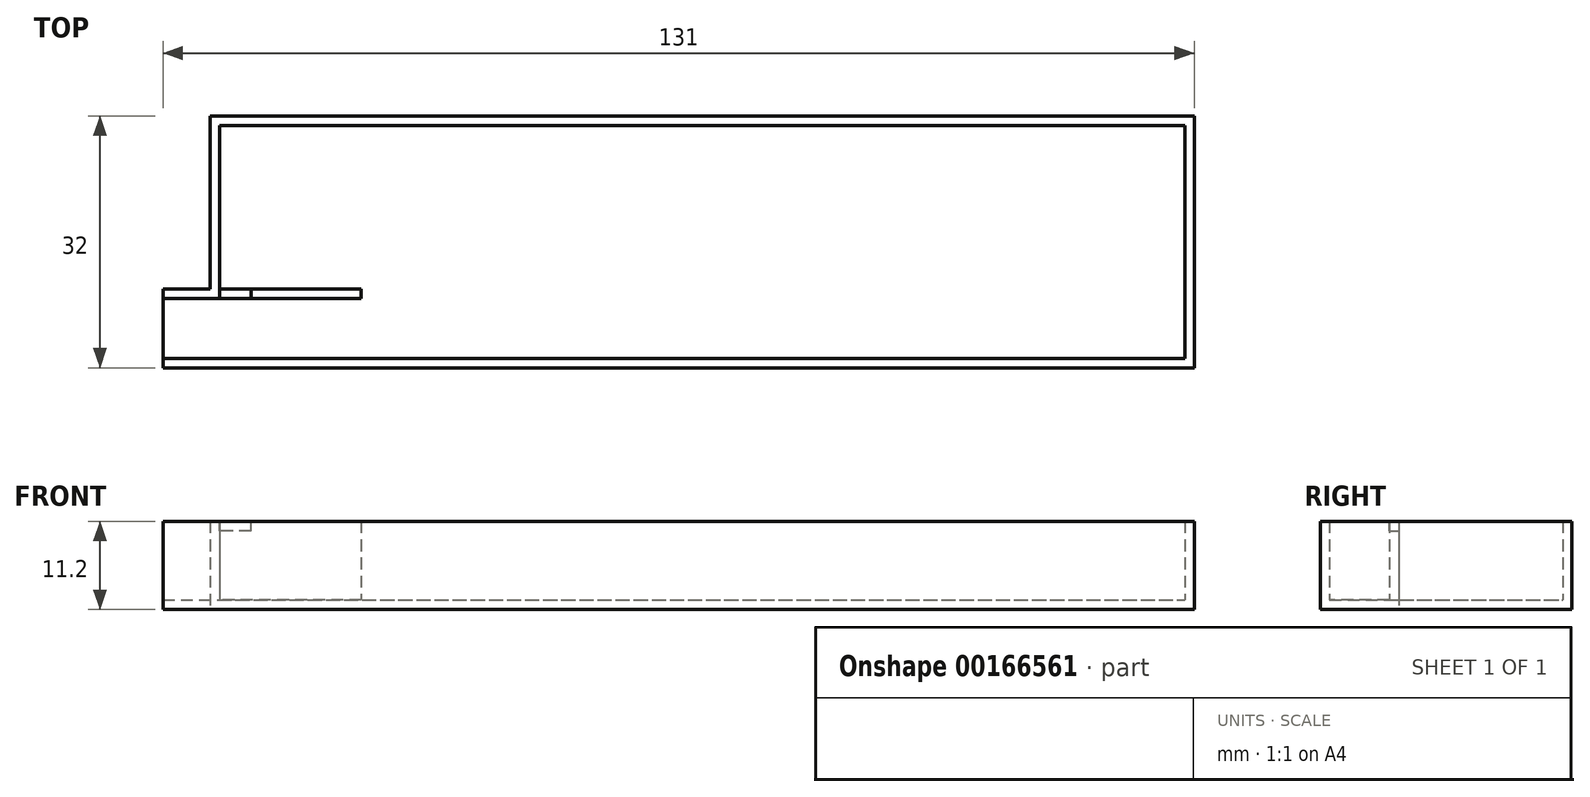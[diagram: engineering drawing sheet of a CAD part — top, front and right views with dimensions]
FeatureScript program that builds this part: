
annotation { "Feature Type Name" : "Feature", "Feature Type Description" : "" }
export const myFeature = defineFeature(function(context is Context, id is Id, definition is map)
    precondition{}
    {
        {
            var Q0;
            Q0=qCreatedBy(makeId("Top.planeOp"),FACE);
            var sketch = newSketch(context, id + "F0", { "sketchPlane" : qUnion([Q0])});
            skLineSegment(sketch, "E0", {"start": v(0, 0) * mm, "end": v(0, 32) * mm});
            skLineSegment(sketch, "E1", {"start": v(0, 32) * mm, "end": v(-125, 32) * mm});
            skLineSegment(sketch, "E2", {"start": v(-125, 32) * mm, "end": v(-125, 10) * mm});
            skLineSegment(sketch, "E3", {"start": v(-125, 10) * mm, "end": v(-131, 10) * mm});
            skLineSegment(sketch, "E4", {"start": v(-131, 10) * mm, "end": v(-131, 0) * mm});
            skLineSegment(sketch, "E5", {"start": v(-131, 0) * mm, "end": v(-125, 0) * mm});
            skLineSegment(sketch, "E6", {"start": v(-125, 0) * mm, "end": v(-125, 0) * mm});
            skLineSegment(sketch, "E7", {"start": v(-125, 0) * mm, "end": v(0, 0) * mm});
            skSolve(sketch);
        }
        {
            var Q0;
            Q0 = qSketchRegion(id + "F0", true);
            extrude(context, id + "F1", {"entities" : qUnion([Q0]), "depth" : 1.2 * mm});
        }
        {
            var Q0;
            Q0=makeQuery(id+"F1.opExtrude","CAP_FACE",FACE,{"disambiguationData":[OSD([sQuery(id+"F0.wireOp",EDGE,"E0"),sQuery(id+"F0.wireOp",EDGE,"E1"),sQuery(id+"F0.wireOp",EDGE,"E2"),sQuery(id+"F0.wireOp",EDGE,"E3"),sQuery(id+"F0.wireOp",EDGE,"E4"),sQuery(id+"F0.wireOp",EDGE,"E5"),sQuery(id+"F0.wireOp",EDGE,"E7")])],"isStart":false});
            var sketch = newSketch(context, id + "F2", { "sketchPlane" : qUnion([Q0])});
            skLineSegment(sketch, "E8", {"start": v(0, 0) * mm, "end": v(-131, 0) * mm});
            skLineSegment(sketch, "E9", {"start": v(-131, 0) * mm, "end": v(-131, 1.2) * mm});
            skLineSegment(sketch, "E10", {"start": v(-131, 10) * mm, "end": v(-131, 8.8) * mm});
            skLineSegment(sketch, "E11", {"start": v(-131, 8.8) * mm, "end": v(-123.8, 8.8) * mm});
            skLineSegment(sketch, "E12", {"start": v(-123.8, 8.8) * mm, "end": v(-123.8, 30.8) * mm});
            skLineSegment(sketch, "E13", {"start": v(-123.8, 30.8) * mm, "end": v(-1.2, 30.8) * mm});
            skLineSegment(sketch, "E14", {"start": v(0, 32) * mm, "end": v(-125, 32) * mm});
            skLineSegment(sketch, "E15", {"start": v(-125, 32) * mm, "end": v(-125, 10) * mm});
            skLineSegment(sketch, "E16", {"start": v(-125, 10) * mm, "end": v(-131, 10) * mm});
            skLineSegment(sketch, "E17", {"start": v(0, 32) * mm, "end": v(0, 0) * mm});
            skLineSegment(sketch, "E18", {"start": v(-131, 1.2) * mm, "end": v(-1.2, 1.2) * mm});
            skLineSegment(sketch, "E19", {"start": v(-1.2, 1.2) * mm, "end": v(-1.2, 30.8) * mm});
            skLineSegment(sketch, "E20", {"start": v(-123.8, 8.8) * mm, "end": v(-105.8, 8.8) * mm});
            skLineSegment(sketch, "E21", {"start": v(-105.8, 8.8) * mm, "end": v(-105.8, 10) * mm});
            skLineSegment(sketch, "E22", {"start": v(-105.8, 10) * mm, "end": v(-123.8, 10) * mm});
            skLineSegment(sketch, "E23", {"start": v(-123.8, 10) * mm, "end": v(-123.8, 8.8) * mm});
            skSolve(sketch);
        }
        {
            var Q0;
            Q0 = qSketchRegion(id + "F2", true);
            extrude(context, id + "F3", {"entities" : qUnion([Q0]), "operationType" : NewBodyOperationType.ADD, "depth" : 10 * mm});
        }
        {
            var Q0;
            Q0=makeQuery(id+"F3.opExtrude","SWEPT_FACE",FACE,{"disambiguationData":[OSD([sQuery(id+"F2.wireOp",EDGE,"E22")])]});
            var sketch = newSketch(context, id + "F4", { "sketchPlane" : qUnion([Q0])});
            skLineSegment(sketch, "E24.bottom", {"start": v(123.8, 11.2) * mm, "end": v(119.8, 11.2) * mm});
            skLineSegment(sketch, "E24.top", {"start": v(123.8, 10) * mm, "end": v(119.8, 10) * mm});
            skLineSegment(sketch, "E24.left", {"start": v(123.8, 11.2) * mm, "end": v(123.8, 10) * mm});
            skLineSegment(sketch, "E24.right", {"start": v(119.8, 11.2) * mm, "end": v(119.8, 10) * mm});
            skSolve(sketch);
        }
        {
            var Q0;
            Q0 = qSketchRegion(id + "F4", true);
            var Q1;
            Q1=makeQuery(id+"F3.opExtrude","SWEPT_FACE",FACE,{"disambiguationData":[OSD([sQuery(id+"F2.wireOp",EDGE,"E11"),sQuery(id+"F2.wireOp",EDGE,"E20")])]});
            extrude(context, id + "F5", {"entities" : qUnion([Q0]), "operationType" : NewBodyOperationType.REMOVE, "endBound" : BoundingType.UP_TO_SURFACE, "oppositeDirection" : true, "endBoundEntityFace" : qUnion([Q1]), "depth" : 25 * mm});
        }
    });
